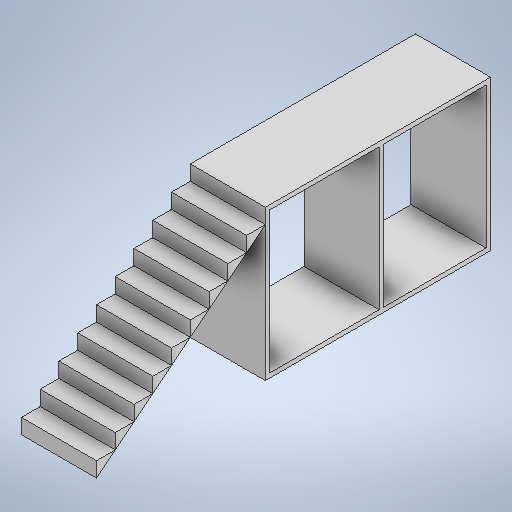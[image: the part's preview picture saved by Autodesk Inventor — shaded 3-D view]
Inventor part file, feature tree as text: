
AUTODESK INVENTOR PART (.ipt)
format: ipt  version: 2025 (Build 290162010, 162A)  size: 285,696 bytes
history: native  units: mm
features: extrude x3, sketch x3, projected_geometry x2, pattern_linear x1
ambient origin geometry x8: Origin, YZ Plane, XZ Plane, XY Plane, X Axis, Y Axis, Z Axis, Center Point
bodies: Solid1 (feature_tree)
feature tree (9):
  extrude  "Extrusion1"  Depth=3000.0mm
  extrude  "Extrusion2"  Depth=250.0mm
  pattern_linear  "Rectangular Pattern1"  Count1=20  [1 undecoded]
  extrude  "Extrusion3"  Depth=60.0mm
  sketch  "Sketch1"  dims[d0=1000.0mm d1=3000.0mm]
  sketch  "Sketch2"  dims[d2=2000.0mm d3=0.0mm d4=250.0mm d5=200.0mm]
  projected_geometry  "Projected Loop1"
  sketch  "Sketch3"  dims[d6=200.0mm d7=8.960554mm d8=2000.0mm d9=0.0mm d10=90.0mm d12=320.0mm d13=60.0mm d14=60.0mm d15=0.0mm d16=0.0mm]
  projected_geometry  "Projected Loop2"
note: 1 required parameter value undecoded (feature->parameter linkage not recoverable at this tier; creation-order binding heuristic only, values carry confidence <= 0.55)
